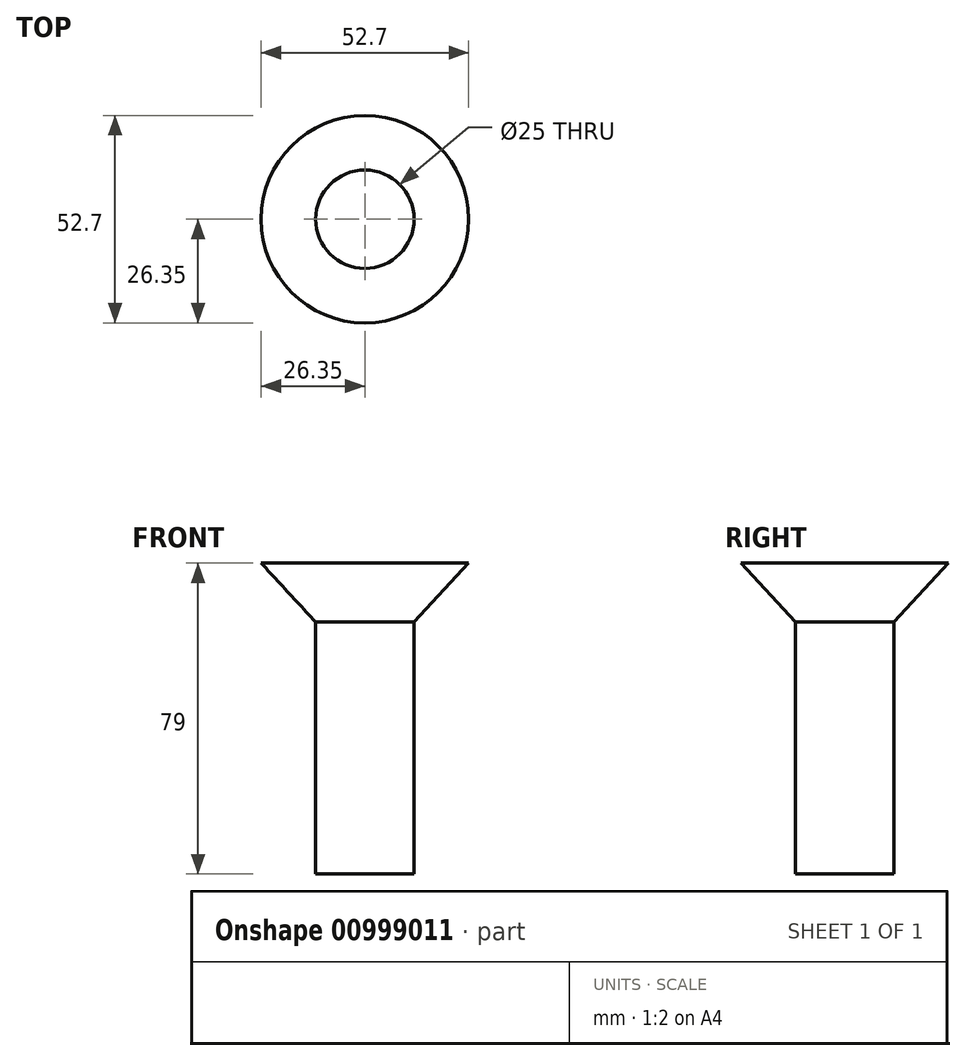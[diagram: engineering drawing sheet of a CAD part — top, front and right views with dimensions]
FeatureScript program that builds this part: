
annotation { "Feature Type Name" : "Feature", "Feature Type Description" : "" }
export const myFeature = defineFeature(function(context is Context, id is Id, definition is map)
    precondition{}
    {
        {
            var Q0;
            Q0=qCreatedBy(makeId("Front.planeOp"),FACE);
            var sketch = newSketch(context, id + "F0", { "sketchPlane" : qUnion([Q0])});
            skLineSegment(sketch, "E0.bottom", {"start": v(12.5, -28.88) * mm, "end": v(0, -28.88) * mm});
            skLineSegment(sketch, "E0.top", {"start": v(12.5, 35.12) * mm, "end": v(0, 35.12) * mm});
            skLineSegment(sketch, "E0.left", {"start": v(12.5, -28.88) * mm, "end": v(12.5, 35.12) * mm});
            skLineSegment(sketch, "E0.right", {"start": v(0, -28.88) * mm, "end": v(0, 35.12) * mm});
            skLineSegment(sketch, "E1", {"start": v(12.5, 35.12) * mm, "end": v(26.35, 50.12) * mm});
            skLineSegment(sketch, "E2", {"start": v(26.35, 50.12) * mm, "end": v(0, 50.12) * mm});
            skLineSegment(sketch, "E3", {"start": v(0, 50.12) * mm, "end": v(0, 35.12) * mm});
            skSolve(sketch);
        }
        {
            var Q0;
            Q0=makeQuery(id+"F0.imprint","IMPRINT",FACE,{"disambiguationData":[TD([[makeQuery(id+"F0.imprint","IMPRINT",EDGE,{"derivedFrom":sQuery(id+"F0.wireOp",EDGE,"E0.bottom")}),-1.0]])]});
            var Q1;
            Q1=sQuery(id+"F0.wireOp",EDGE,"E0.left");
            var Q2;
            Q2=sQuery(id+"F0.wireOp",EDGE,"E0.right");
            revolve(context, id + "F1", {"bodyType" : ToolBodyType.SURFACE, "surfaceOperationType" : NewSurfaceOperationType.NEW, "entities" : qUnion([Q0]), "surfaceEntities" : qUnion([Q1]), "axis" : qUnion([Q2]), "revolveType" : RevolveType.FULL});
        }
        {
            var Q0;
            Q0=makeQuery(id+"F0.imprint","IMPRINT",FACE,{"disambiguationData":[TD([[makeQuery(id+"F0.imprint","IMPRINT",EDGE,{"derivedFrom":sQuery(id+"F0.wireOp",EDGE,"E0.top")}),-1.0]])]});
            var Q1;
            Q1=sQuery(id+"F0.wireOp",EDGE,"E1");
            var Q2;
            Q2=sQuery(id+"F0.wireOp",EDGE,"E3");
            revolve(context, id + "F2", {"bodyType" : ToolBodyType.SURFACE, "operationType" : NewBodyOperationType.ADD, "surfaceOperationType" : NewSurfaceOperationType.NEW, "entities" : qUnion([Q0]), "surfaceEntities" : qUnion([Q1]), "axis" : qUnion([Q2]), "revolveType" : RevolveType.FULL});
        }
    });
